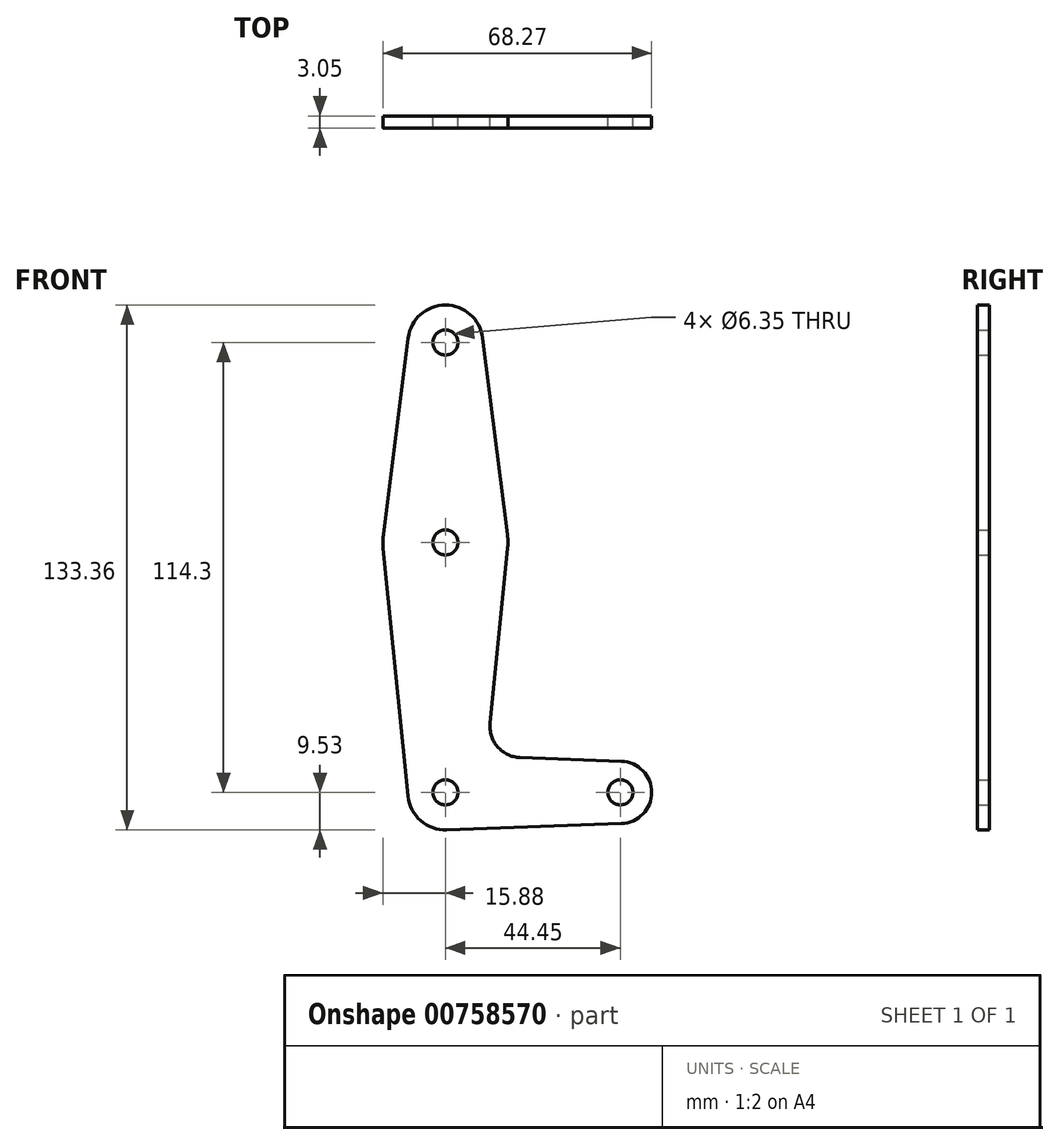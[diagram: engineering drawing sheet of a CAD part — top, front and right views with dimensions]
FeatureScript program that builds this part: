
annotation { "Feature Type Name" : "Feature", "Feature Type Description" : "" }
export const myFeature = defineFeature(function(context is Context, id is Id, definition is map)
    precondition{}
    {
        {
            var Q0;
            Q0=qCreatedBy(makeId("Front.planeOp"),FACE);
            var sketch = newSketch(context, id + "F0", { "sketchPlane" : qUnion([Q0])});
            skLineSegment(sketch, "E0", {"start": v(0, 0) * mm, "end": v(0, -50.8) * mm, "construction": true});
            skLineSegment(sketch, "E1", {"start": v(0, -50.8) * mm, "end": v(0, -114.3) * mm, "construction": true});
            skLineSegment(sketch, "E2", {"start": v(0, -114.3) * mm, "end": v(44.45, -114.3) * mm, "construction": true});
            skCircle(sketch, "E3", {"center": v(0, 0) * mm, "radius": 9.53 * mm});
            skCircle(sketch, "E4", {"center": v(0, -50.8) * mm, "radius": 15.88 * mm});
            skCircle(sketch, "E5", {"center": v(0, -114.3) * mm, "radius": 9.53 * mm});
            skCircle(sketch, "E6", {"center": v(44.45, -114.3) * mm, "radius": 7.94 * mm});
            skLineSegment(sketch, "E7", {"start": v(9.45, 1.2) * mm, "end": v(15.75, -48.82) * mm});
            skLineSegment(sketch, "E8", {"start": v(-9.45, 1.2) * mm, "end": v(-15.75, -48.82) * mm});
            skLineSegment(sketch, "E9", {"start": v(-15.8, -52.39) * mm, "end": v(-9.48, -115.25) * mm});
            skLineSegment(sketch, "E10", {"start": v(18.97, -105.45) * mm, "end": v(44.73, -106.37) * mm});
            skLineSegment(sketch, "E11", {"start": v(11.34, -96.7) * mm, "end": v(15.8, -52.39) * mm});
            skLineSegment(sketch, "E12", {"start": v(0.34, -123.82) * mm, "end": v(44.73, -122.23) * mm});
            skArc(sketch, "E13.filletArc", {"start": v(11.34, -96.7) * mm, "mid": v(13.26, -102.73) * mm, "end": v(18.97, -105.45) * mm});
            skCircle(sketch, "E14", {"center": v(0, 0) * mm, "radius": 3.18 * mm});
            skCircle(sketch, "E15", {"center": v(0, -50.8) * mm, "radius": 3.18 * mm});
            skCircle(sketch, "E16", {"center": v(0, -114.3) * mm, "radius": 3.18 * mm});
            skCircle(sketch, "E17", {"center": v(44.45, -114.3) * mm, "radius": 3.18 * mm});
            skSolve(sketch);
        }
        {
            var Q0;
            Q0 = qSketchRegion(id + "F0", true);
            extrude(context, id + "F1", {"entities" : qUnion([Q0]), "depth" : 3.05 * mm, "offsetDistance" : 25.4 * mm});
        }
    });
